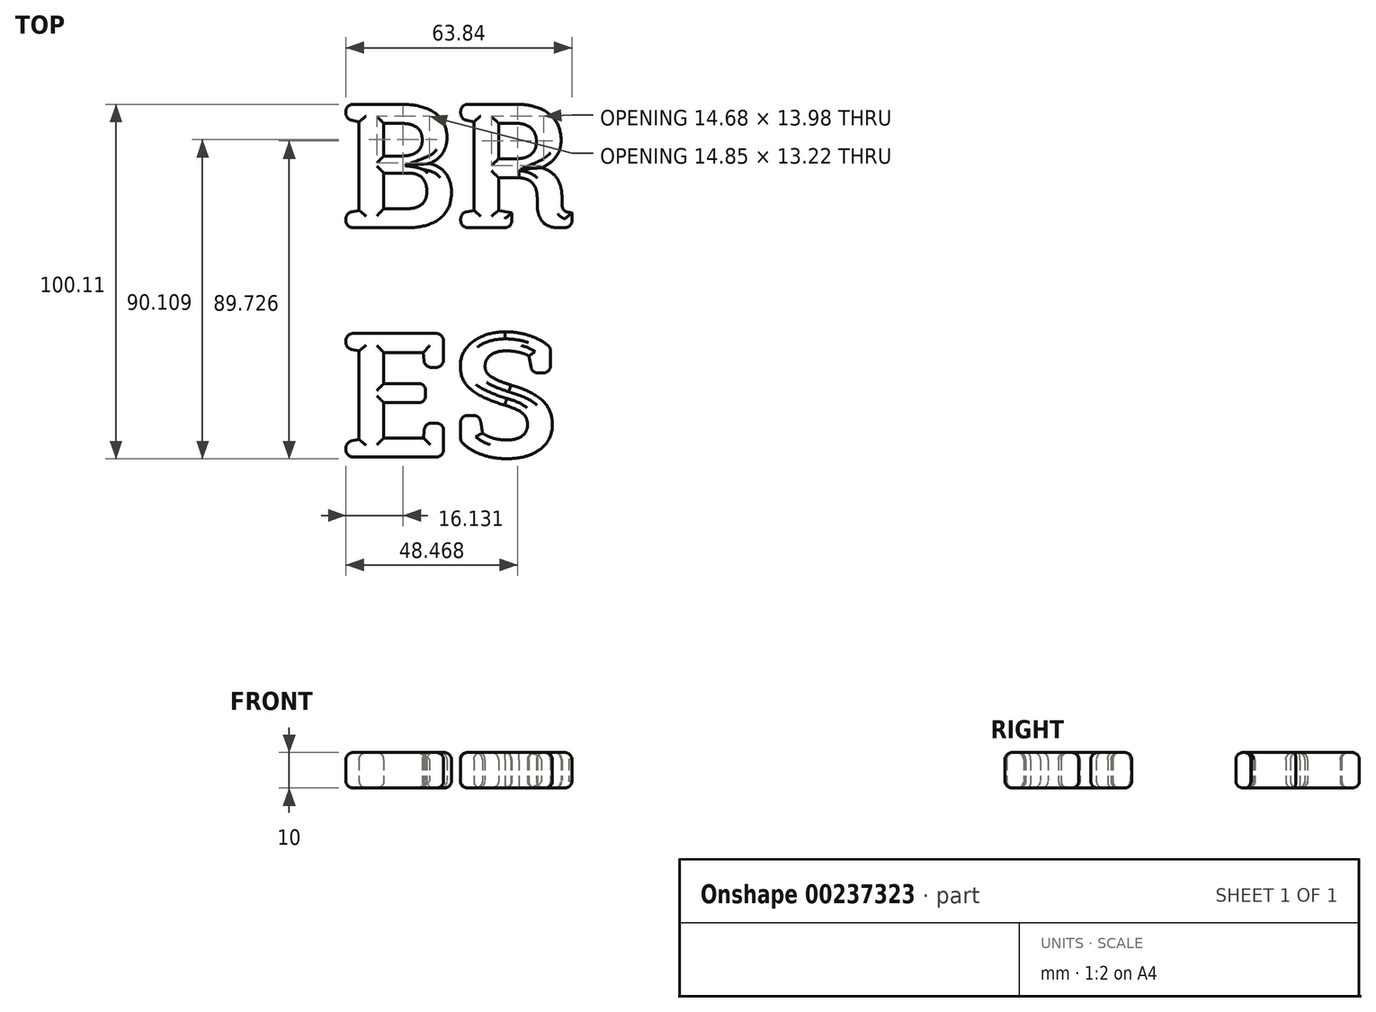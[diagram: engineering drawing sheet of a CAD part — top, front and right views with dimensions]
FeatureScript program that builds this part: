
annotation { "Feature Type Name" : "Feature", "Feature Type Description" : "" }
export const myFeature = defineFeature(function(context is Context, id is Id, definition is map)
    precondition{}
    {
        {
            var Q0;
            Q0=qCreatedBy(makeId("Top.planeOp"),FACE);
            var sketch = newSketch(context, id + "F0", { "sketchPlane" : qUnion([Q0])});
            skText(sketch, "E0", { "text": "BR\nES", "fontName": "RobotoSlab-Bold.ttf"});
            const initialGuessF0  = {"E0": [0, 0, 1, 0, 0.03531]};
            skSetInitialGuess(sketch, initialGuessF0);
            skSolve(sketch);
        }
        {
            var Q0;
            Q0 = qSketchRegion(id + "F0", true);
            extrude(context, id + "F1", {"entities" : qUnion([Q0]), "depth" : 10 * mm});
        }
        {
            var Q0;
            Q0=makeQuery(id+"F1.opExtrude","CAP_FACE",FACE,{"disambiguationData":[OSD([sQuery(id+"F0.wireOp",EDGE,"E0.sketch_text.stroke-0"),sQuery(id+"F0.wireOp",EDGE,"E0.sketch_text.stroke-1"),sQuery(id+"F0.wireOp",EDGE,"E0.sketch_text.stroke-2"),sQuery(id+"F0.wireOp",EDGE,"E0.sketch_text.stroke-3"),sQuery(id+"F0.wireOp",EDGE,"E0.sketch_text.stroke-4"),sQuery(id+"F0.wireOp",EDGE,"E0.sketch_text.stroke-5"),sQuery(id+"F0.wireOp",EDGE,"E0.sketch_text.stroke-6"),sQuery(id+"F0.wireOp",EDGE,"E0.sketch_text.stroke-7"),sQuery(id+"F0.wireOp",EDGE,"E0.sketch_text.stroke-8"),sQuery(id+"F0.wireOp",EDGE,"E0.sketch_text.stroke-9"),sQuery(id+"F0.wireOp",EDGE,"E0.sketch_text.stroke-10"),sQuery(id+"F0.wireOp",EDGE,"E0.sketch_text.stroke-11"),sQuery(id+"F0.wireOp",EDGE,"E0.sketch_text.stroke-12"),sQuery(id+"F0.wireOp",EDGE,"E0.sketch_text.stroke-13"),sQuery(id+"F0.wireOp",EDGE,"E0.sketch_text.stroke-14"),sQuery(id+"F0.wireOp",EDGE,"E0.sketch_text.stroke-15"),sQuery(id+"F0.wireOp",EDGE,"E0.sketch_text.stroke-16"),sQuery(id+"F0.wireOp",EDGE,"E0.sketch_text.stroke-17"),sQuery(id+"F0.wireOp",EDGE,"E0.sketch_text.stroke-18"),sQuery(id+"F0.wireOp",EDGE,"E0.sketch_text.stroke-19"),sQuery(id+"F0.wireOp",EDGE,"E0.sketch_text.stroke-20"),sQuery(id+"F0.wireOp",EDGE,"E0.sketch_text.stroke-21"),sQuery(id+"F0.wireOp",EDGE,"E0.sketch_text.stroke-22"),sQuery(id+"F0.wireOp",EDGE,"E0.sketch_text.stroke-23"),sQuery(id+"F0.wireOp",EDGE,"E0.sketch_text.stroke-24"),sQuery(id+"F0.wireOp",EDGE,"E0.sketch_text.stroke-25"),sQuery(id+"F0.wireOp",EDGE,"E0.sketch_text.stroke-26"),sQuery(id+"F0.wireOp",EDGE,"E0.sketch_text.stroke-27"),sQuery(id+"F0.wireOp",EDGE,"E0.sketch_text.stroke-28"),sQuery(id+"F0.wireOp",EDGE,"E0.sketch_text.stroke-29")])],"isStart":false});
            var Q1;
            Q1=makeQuery(id+"F1.opExtrude","CAP_FACE",FACE,{"disambiguationData":[OSD([sQuery(id+"F0.wireOp",EDGE,"E0.sketch_text.stroke-0"),sQuery(id+"F0.wireOp",EDGE,"E0.sketch_text.stroke-1"),sQuery(id+"F0.wireOp",EDGE,"E0.sketch_text.stroke-2"),sQuery(id+"F0.wireOp",EDGE,"E0.sketch_text.stroke-3"),sQuery(id+"F0.wireOp",EDGE,"E0.sketch_text.stroke-4"),sQuery(id+"F0.wireOp",EDGE,"E0.sketch_text.stroke-5"),sQuery(id+"F0.wireOp",EDGE,"E0.sketch_text.stroke-6"),sQuery(id+"F0.wireOp",EDGE,"E0.sketch_text.stroke-7"),sQuery(id+"F0.wireOp",EDGE,"E0.sketch_text.stroke-8"),sQuery(id+"F0.wireOp",EDGE,"E0.sketch_text.stroke-9"),sQuery(id+"F0.wireOp",EDGE,"E0.sketch_text.stroke-10"),sQuery(id+"F0.wireOp",EDGE,"E0.sketch_text.stroke-11"),sQuery(id+"F0.wireOp",EDGE,"E0.sketch_text.stroke-12"),sQuery(id+"F0.wireOp",EDGE,"E0.sketch_text.stroke-13"),sQuery(id+"F0.wireOp",EDGE,"E0.sketch_text.stroke-14"),sQuery(id+"F0.wireOp",EDGE,"E0.sketch_text.stroke-15"),sQuery(id+"F0.wireOp",EDGE,"E0.sketch_text.stroke-16"),sQuery(id+"F0.wireOp",EDGE,"E0.sketch_text.stroke-17"),sQuery(id+"F0.wireOp",EDGE,"E0.sketch_text.stroke-18"),sQuery(id+"F0.wireOp",EDGE,"E0.sketch_text.stroke-19"),sQuery(id+"F0.wireOp",EDGE,"E0.sketch_text.stroke-20"),sQuery(id+"F0.wireOp",EDGE,"E0.sketch_text.stroke-21"),sQuery(id+"F0.wireOp",EDGE,"E0.sketch_text.stroke-22"),sQuery(id+"F0.wireOp",EDGE,"E0.sketch_text.stroke-23"),sQuery(id+"F0.wireOp",EDGE,"E0.sketch_text.stroke-24"),sQuery(id+"F0.wireOp",EDGE,"E0.sketch_text.stroke-25"),sQuery(id+"F0.wireOp",EDGE,"E0.sketch_text.stroke-26"),sQuery(id+"F0.wireOp",EDGE,"E0.sketch_text.stroke-27"),sQuery(id+"F0.wireOp",EDGE,"E0.sketch_text.stroke-28"),sQuery(id+"F0.wireOp",EDGE,"E0.sketch_text.stroke-29")])],"isStart":true});
            var Q2;
            Q2=makeQuery(id+"F1.opExtrude","SWEPT_FACE",FACE,{"disambiguationData":[OSD([sQuery(id+"F0.wireOp",EDGE,"E0.sketch_text.stroke-13")])]});
            var Q3;
            Q3=makeQuery(id+"F1.opExtrude","SWEPT_FACE",FACE,{"disambiguationData":[OSD([sQuery(id+"F0.wireOp",EDGE,"E0.sketch_text.stroke-9")])]});
            var Q4;
            Q4=makeQuery(id+"F1.opExtrude","CAP_FACE",FACE,{"disambiguationData":[OSD([sQuery(id+"F0.wireOp",EDGE,"E0.sketch_text.stroke-30"),sQuery(id+"F0.wireOp",EDGE,"E0.sketch_text.stroke-31"),sQuery(id+"F0.wireOp",EDGE,"E0.sketch_text.stroke-32"),sQuery(id+"F0.wireOp",EDGE,"E0.sketch_text.stroke-33"),sQuery(id+"F0.wireOp",EDGE,"E0.sketch_text.stroke-34"),sQuery(id+"F0.wireOp",EDGE,"E0.sketch_text.stroke-35"),sQuery(id+"F0.wireOp",EDGE,"E0.sketch_text.stroke-36"),sQuery(id+"F0.wireOp",EDGE,"E0.sketch_text.stroke-37"),sQuery(id+"F0.wireOp",EDGE,"E0.sketch_text.stroke-38"),sQuery(id+"F0.wireOp",EDGE,"E0.sketch_text.stroke-39"),sQuery(id+"F0.wireOp",EDGE,"E0.sketch_text.stroke-40"),sQuery(id+"F0.wireOp",EDGE,"E0.sketch_text.stroke-41"),sQuery(id+"F0.wireOp",EDGE,"E0.sketch_text.stroke-42"),sQuery(id+"F0.wireOp",EDGE,"E0.sketch_text.stroke-43"),sQuery(id+"F0.wireOp",EDGE,"E0.sketch_text.stroke-44"),sQuery(id+"F0.wireOp",EDGE,"E0.sketch_text.stroke-45"),sQuery(id+"F0.wireOp",EDGE,"E0.sketch_text.stroke-46"),sQuery(id+"F0.wireOp",EDGE,"E0.sketch_text.stroke-47"),sQuery(id+"F0.wireOp",EDGE,"E0.sketch_text.stroke-48"),sQuery(id+"F0.wireOp",EDGE,"E0.sketch_text.stroke-49"),sQuery(id+"F0.wireOp",EDGE,"E0.sketch_text.stroke-50"),sQuery(id+"F0.wireOp",EDGE,"E0.sketch_text.stroke-51"),sQuery(id+"F0.wireOp",EDGE,"E0.sketch_text.stroke-52"),sQuery(id+"F0.wireOp",EDGE,"E0.sketch_text.stroke-53"),sQuery(id+"F0.wireOp",EDGE,"E0.sketch_text.stroke-54"),sQuery(id+"F0.wireOp",EDGE,"E0.sketch_text.stroke-55"),sQuery(id+"F0.wireOp",EDGE,"E0.sketch_text.stroke-56"),sQuery(id+"F0.wireOp",EDGE,"E0.sketch_text.stroke-57"),sQuery(id+"F0.wireOp",EDGE,"E0.sketch_text.stroke-58"),sQuery(id+"F0.wireOp",EDGE,"E0.sketch_text.stroke-59"),sQuery(id+"F0.wireOp",EDGE,"E0.sketch_text.stroke-60"),sQuery(id+"F0.wireOp",EDGE,"E0.sketch_text.stroke-61"),sQuery(id+"F0.wireOp",EDGE,"E0.sketch_text.stroke-62"),sQuery(id+"F0.wireOp",EDGE,"E0.sketch_text.stroke-63"),sQuery(id+"F0.wireOp",EDGE,"E0.sketch_text.stroke-64"),sQuery(id+"F0.wireOp",EDGE,"E0.sketch_text.stroke-65")])],"isStart":false});
            var Q5;
            Q5=makeQuery(id+"F1.opExtrude","CAP_FACE",FACE,{"disambiguationData":[OSD([sQuery(id+"F0.wireOp",EDGE,"E0.sketch_text.stroke-30"),sQuery(id+"F0.wireOp",EDGE,"E0.sketch_text.stroke-31"),sQuery(id+"F0.wireOp",EDGE,"E0.sketch_text.stroke-32"),sQuery(id+"F0.wireOp",EDGE,"E0.sketch_text.stroke-33"),sQuery(id+"F0.wireOp",EDGE,"E0.sketch_text.stroke-34"),sQuery(id+"F0.wireOp",EDGE,"E0.sketch_text.stroke-35"),sQuery(id+"F0.wireOp",EDGE,"E0.sketch_text.stroke-36"),sQuery(id+"F0.wireOp",EDGE,"E0.sketch_text.stroke-37"),sQuery(id+"F0.wireOp",EDGE,"E0.sketch_text.stroke-38"),sQuery(id+"F0.wireOp",EDGE,"E0.sketch_text.stroke-39"),sQuery(id+"F0.wireOp",EDGE,"E0.sketch_text.stroke-40"),sQuery(id+"F0.wireOp",EDGE,"E0.sketch_text.stroke-41"),sQuery(id+"F0.wireOp",EDGE,"E0.sketch_text.stroke-42"),sQuery(id+"F0.wireOp",EDGE,"E0.sketch_text.stroke-43"),sQuery(id+"F0.wireOp",EDGE,"E0.sketch_text.stroke-44"),sQuery(id+"F0.wireOp",EDGE,"E0.sketch_text.stroke-45"),sQuery(id+"F0.wireOp",EDGE,"E0.sketch_text.stroke-46"),sQuery(id+"F0.wireOp",EDGE,"E0.sketch_text.stroke-47"),sQuery(id+"F0.wireOp",EDGE,"E0.sketch_text.stroke-48"),sQuery(id+"F0.wireOp",EDGE,"E0.sketch_text.stroke-49"),sQuery(id+"F0.wireOp",EDGE,"E0.sketch_text.stroke-50"),sQuery(id+"F0.wireOp",EDGE,"E0.sketch_text.stroke-51"),sQuery(id+"F0.wireOp",EDGE,"E0.sketch_text.stroke-52"),sQuery(id+"F0.wireOp",EDGE,"E0.sketch_text.stroke-53"),sQuery(id+"F0.wireOp",EDGE,"E0.sketch_text.stroke-54"),sQuery(id+"F0.wireOp",EDGE,"E0.sketch_text.stroke-55"),sQuery(id+"F0.wireOp",EDGE,"E0.sketch_text.stroke-56"),sQuery(id+"F0.wireOp",EDGE,"E0.sketch_text.stroke-57"),sQuery(id+"F0.wireOp",EDGE,"E0.sketch_text.stroke-58"),sQuery(id+"F0.wireOp",EDGE,"E0.sketch_text.stroke-59"),sQuery(id+"F0.wireOp",EDGE,"E0.sketch_text.stroke-60"),sQuery(id+"F0.wireOp",EDGE,"E0.sketch_text.stroke-61"),sQuery(id+"F0.wireOp",EDGE,"E0.sketch_text.stroke-62"),sQuery(id+"F0.wireOp",EDGE,"E0.sketch_text.stroke-63"),sQuery(id+"F0.wireOp",EDGE,"E0.sketch_text.stroke-64"),sQuery(id+"F0.wireOp",EDGE,"E0.sketch_text.stroke-65")])],"isStart":true});
            var Q6;
            Q6=makeQuery(id+"F1.opExtrude","SWEPT_FACE",FACE,{"disambiguationData":[OSD([sQuery(id+"F0.wireOp",EDGE,"E0.sketch_text.stroke-51")])]});
            var Q7;
            Q7=makeQuery(id+"F1.opExtrude","SWEPT_FACE",FACE,{"disambiguationData":[OSD([sQuery(id+"F0.wireOp",EDGE,"E0.sketch_text.stroke-52")])]});
            var Q8;
            Q8=makeQuery(id+"F1.opExtrude","SWEPT_FACE",FACE,{"disambiguationData":[OSD([sQuery(id+"F0.wireOp",EDGE,"E0.sketch_text.stroke-56")])]});
            var Q9;
            Q9=makeQuery(id+"F1.opExtrude","SWEPT_EDGE",EDGE,{"disambiguationData":[OSD([sQuery(id+"F0.wireOp",EDGE,"E0.sketch_text.stroke-40"),sQuery(id+"F0.wireOp",EDGE,"E0.sketch_text.stroke-41")])]});
            var Q10;
            Q10=makeQuery(id+"F1.opExtrude","CAP_FACE",FACE,{"disambiguationData":[OSD([sQuery(id+"F0.wireOp",EDGE,"E0.sketch_text.stroke-66"),sQuery(id+"F0.wireOp",EDGE,"E0.sketch_text.stroke-67"),sQuery(id+"F0.wireOp",EDGE,"E0.sketch_text.stroke-68"),sQuery(id+"F0.wireOp",EDGE,"E0.sketch_text.stroke-69"),sQuery(id+"F0.wireOp",EDGE,"E0.sketch_text.stroke-70"),sQuery(id+"F0.wireOp",EDGE,"E0.sketch_text.stroke-71"),sQuery(id+"F0.wireOp",EDGE,"E0.sketch_text.stroke-72"),sQuery(id+"F0.wireOp",EDGE,"E0.sketch_text.stroke-73"),sQuery(id+"F0.wireOp",EDGE,"E0.sketch_text.stroke-74"),sQuery(id+"F0.wireOp",EDGE,"E0.sketch_text.stroke-75"),sQuery(id+"F0.wireOp",EDGE,"E0.sketch_text.stroke-76"),sQuery(id+"F0.wireOp",EDGE,"E0.sketch_text.stroke-77"),sQuery(id+"F0.wireOp",EDGE,"E0.sketch_text.stroke-78"),sQuery(id+"F0.wireOp",EDGE,"E0.sketch_text.stroke-79"),sQuery(id+"F0.wireOp",EDGE,"E0.sketch_text.stroke-80"),sQuery(id+"F0.wireOp",EDGE,"E0.sketch_text.stroke-81"),sQuery(id+"F0.wireOp",EDGE,"E0.sketch_text.stroke-82"),sQuery(id+"F0.wireOp",EDGE,"E0.sketch_text.stroke-83"),sQuery(id+"F0.wireOp",EDGE,"E0.sketch_text.stroke-84"),sQuery(id+"F0.wireOp",EDGE,"E0.sketch_text.stroke-85"),sQuery(id+"F0.wireOp",EDGE,"E0.sketch_text.stroke-86")])],"isStart":false});
            var Q11;
            Q11=makeQuery(id+"F1.opExtrude","CAP_FACE",FACE,{"disambiguationData":[OSD([sQuery(id+"F0.wireOp",EDGE,"E0.sketch_text.stroke-87"),sQuery(id+"F0.wireOp",EDGE,"E0.sketch_text.stroke-88"),sQuery(id+"F0.wireOp",EDGE,"E0.sketch_text.stroke-89"),sQuery(id+"F0.wireOp",EDGE,"E0.sketch_text.stroke-90"),sQuery(id+"F0.wireOp",EDGE,"E0.sketch_text.stroke-91"),sQuery(id+"F0.wireOp",EDGE,"E0.sketch_text.stroke-92"),sQuery(id+"F0.wireOp",EDGE,"E0.sketch_text.stroke-93"),sQuery(id+"F0.wireOp",EDGE,"E0.sketch_text.stroke-94"),sQuery(id+"F0.wireOp",EDGE,"E0.sketch_text.stroke-95"),sQuery(id+"F0.wireOp",EDGE,"E0.sketch_text.stroke-96"),sQuery(id+"F0.wireOp",EDGE,"E0.sketch_text.stroke-97"),sQuery(id+"F0.wireOp",EDGE,"E0.sketch_text.stroke-98"),sQuery(id+"F0.wireOp",EDGE,"E0.sketch_text.stroke-99"),sQuery(id+"F0.wireOp",EDGE,"E0.sketch_text.stroke-100"),sQuery(id+"F0.wireOp",EDGE,"E0.sketch_text.stroke-101"),sQuery(id+"F0.wireOp",EDGE,"E0.sketch_text.stroke-102"),sQuery(id+"F0.wireOp",EDGE,"E0.sketch_text.stroke-103"),sQuery(id+"F0.wireOp",EDGE,"E0.sketch_text.stroke-104"),sQuery(id+"F0.wireOp",EDGE,"E0.sketch_text.stroke-105"),sQuery(id+"F0.wireOp",EDGE,"E0.sketch_text.stroke-106"),sQuery(id+"F0.wireOp",EDGE,"E0.sketch_text.stroke-107"),sQuery(id+"F0.wireOp",EDGE,"E0.sketch_text.stroke-108"),sQuery(id+"F0.wireOp",EDGE,"E0.sketch_text.stroke-109"),sQuery(id+"F0.wireOp",EDGE,"E0.sketch_text.stroke-110"),sQuery(id+"F0.wireOp",EDGE,"E0.sketch_text.stroke-111"),sQuery(id+"F0.wireOp",EDGE,"E0.sketch_text.stroke-112"),sQuery(id+"F0.wireOp",EDGE,"E0.sketch_text.stroke-113"),sQuery(id+"F0.wireOp",EDGE,"E0.sketch_text.stroke-114"),sQuery(id+"F0.wireOp",EDGE,"E0.sketch_text.stroke-115"),sQuery(id+"F0.wireOp",EDGE,"E0.sketch_text.stroke-116")])],"isStart":false});
            var Q12;
            Q12=makeQuery(id+"F1.opExtrude","CAP_FACE",FACE,{"disambiguationData":[OSD([sQuery(id+"F0.wireOp",EDGE,"E0.sketch_text.stroke-117"),sQuery(id+"F0.wireOp",EDGE,"E0.sketch_text.stroke-118"),sQuery(id+"F0.wireOp",EDGE,"E0.sketch_text.stroke-119"),sQuery(id+"F0.wireOp",EDGE,"E0.sketch_text.stroke-120"),sQuery(id+"F0.wireOp",EDGE,"E0.sketch_text.stroke-121"),sQuery(id+"F0.wireOp",EDGE,"E0.sketch_text.stroke-122"),sQuery(id+"F0.wireOp",EDGE,"E0.sketch_text.stroke-123"),sQuery(id+"F0.wireOp",EDGE,"E0.sketch_text.stroke-124"),sQuery(id+"F0.wireOp",EDGE,"E0.sketch_text.stroke-125"),sQuery(id+"F0.wireOp",EDGE,"E0.sketch_text.stroke-126"),sQuery(id+"F0.wireOp",EDGE,"E0.sketch_text.stroke-127"),sQuery(id+"F0.wireOp",EDGE,"E0.sketch_text.stroke-128"),sQuery(id+"F0.wireOp",EDGE,"E0.sketch_text.stroke-129"),sQuery(id+"F0.wireOp",EDGE,"E0.sketch_text.stroke-130"),sQuery(id+"F0.wireOp",EDGE,"E0.sketch_text.stroke-131"),sQuery(id+"F0.wireOp",EDGE,"E0.sketch_text.stroke-132"),sQuery(id+"F0.wireOp",EDGE,"E0.sketch_text.stroke-133"),sQuery(id+"F0.wireOp",EDGE,"E0.sketch_text.stroke-134"),sQuery(id+"F0.wireOp",EDGE,"E0.sketch_text.stroke-135"),sQuery(id+"F0.wireOp",EDGE,"E0.sketch_text.stroke-136"),sQuery(id+"F0.wireOp",EDGE,"E0.sketch_text.stroke-137"),sQuery(id+"F0.wireOp",EDGE,"E0.sketch_text.stroke-138"),sQuery(id+"F0.wireOp",EDGE,"E0.sketch_text.stroke-139"),sQuery(id+"F0.wireOp",EDGE,"E0.sketch_text.stroke-140"),sQuery(id+"F0.wireOp",EDGE,"E0.sketch_text.stroke-141"),sQuery(id+"F0.wireOp",EDGE,"E0.sketch_text.stroke-142"),sQuery(id+"F0.wireOp",EDGE,"E0.sketch_text.stroke-143"),sQuery(id+"F0.wireOp",EDGE,"E0.sketch_text.stroke-144"),sQuery(id+"F0.wireOp",EDGE,"E0.sketch_text.stroke-145"),sQuery(id+"F0.wireOp",EDGE,"E0.sketch_text.stroke-146")])],"isStart":false});
            var Q13;
            Q13=makeQuery(id+"F1.opExtrude","CAP_FACE",FACE,{"disambiguationData":[OSD([sQuery(id+"F0.wireOp",EDGE,"E0.sketch_text.stroke-66"),sQuery(id+"F0.wireOp",EDGE,"E0.sketch_text.stroke-67"),sQuery(id+"F0.wireOp",EDGE,"E0.sketch_text.stroke-68"),sQuery(id+"F0.wireOp",EDGE,"E0.sketch_text.stroke-69"),sQuery(id+"F0.wireOp",EDGE,"E0.sketch_text.stroke-70"),sQuery(id+"F0.wireOp",EDGE,"E0.sketch_text.stroke-71"),sQuery(id+"F0.wireOp",EDGE,"E0.sketch_text.stroke-72"),sQuery(id+"F0.wireOp",EDGE,"E0.sketch_text.stroke-73"),sQuery(id+"F0.wireOp",EDGE,"E0.sketch_text.stroke-74"),sQuery(id+"F0.wireOp",EDGE,"E0.sketch_text.stroke-75"),sQuery(id+"F0.wireOp",EDGE,"E0.sketch_text.stroke-76"),sQuery(id+"F0.wireOp",EDGE,"E0.sketch_text.stroke-77"),sQuery(id+"F0.wireOp",EDGE,"E0.sketch_text.stroke-78"),sQuery(id+"F0.wireOp",EDGE,"E0.sketch_text.stroke-79"),sQuery(id+"F0.wireOp",EDGE,"E0.sketch_text.stroke-80"),sQuery(id+"F0.wireOp",EDGE,"E0.sketch_text.stroke-81"),sQuery(id+"F0.wireOp",EDGE,"E0.sketch_text.stroke-82"),sQuery(id+"F0.wireOp",EDGE,"E0.sketch_text.stroke-83"),sQuery(id+"F0.wireOp",EDGE,"E0.sketch_text.stroke-84"),sQuery(id+"F0.wireOp",EDGE,"E0.sketch_text.stroke-85"),sQuery(id+"F0.wireOp",EDGE,"E0.sketch_text.stroke-86")])],"isStart":true});
            var Q14;
            Q14=makeQuery(id+"F1.opExtrude","CAP_FACE",FACE,{"disambiguationData":[OSD([sQuery(id+"F0.wireOp",EDGE,"E0.sketch_text.stroke-87"),sQuery(id+"F0.wireOp",EDGE,"E0.sketch_text.stroke-88"),sQuery(id+"F0.wireOp",EDGE,"E0.sketch_text.stroke-89"),sQuery(id+"F0.wireOp",EDGE,"E0.sketch_text.stroke-90"),sQuery(id+"F0.wireOp",EDGE,"E0.sketch_text.stroke-91"),sQuery(id+"F0.wireOp",EDGE,"E0.sketch_text.stroke-92"),sQuery(id+"F0.wireOp",EDGE,"E0.sketch_text.stroke-93"),sQuery(id+"F0.wireOp",EDGE,"E0.sketch_text.stroke-94"),sQuery(id+"F0.wireOp",EDGE,"E0.sketch_text.stroke-95"),sQuery(id+"F0.wireOp",EDGE,"E0.sketch_text.stroke-96"),sQuery(id+"F0.wireOp",EDGE,"E0.sketch_text.stroke-97"),sQuery(id+"F0.wireOp",EDGE,"E0.sketch_text.stroke-98"),sQuery(id+"F0.wireOp",EDGE,"E0.sketch_text.stroke-99"),sQuery(id+"F0.wireOp",EDGE,"E0.sketch_text.stroke-100"),sQuery(id+"F0.wireOp",EDGE,"E0.sketch_text.stroke-101"),sQuery(id+"F0.wireOp",EDGE,"E0.sketch_text.stroke-102"),sQuery(id+"F0.wireOp",EDGE,"E0.sketch_text.stroke-103"),sQuery(id+"F0.wireOp",EDGE,"E0.sketch_text.stroke-104"),sQuery(id+"F0.wireOp",EDGE,"E0.sketch_text.stroke-105"),sQuery(id+"F0.wireOp",EDGE,"E0.sketch_text.stroke-106"),sQuery(id+"F0.wireOp",EDGE,"E0.sketch_text.stroke-107"),sQuery(id+"F0.wireOp",EDGE,"E0.sketch_text.stroke-108"),sQuery(id+"F0.wireOp",EDGE,"E0.sketch_text.stroke-109"),sQuery(id+"F0.wireOp",EDGE,"E0.sketch_text.stroke-110"),sQuery(id+"F0.wireOp",EDGE,"E0.sketch_text.stroke-111"),sQuery(id+"F0.wireOp",EDGE,"E0.sketch_text.stroke-112"),sQuery(id+"F0.wireOp",EDGE,"E0.sketch_text.stroke-113"),sQuery(id+"F0.wireOp",EDGE,"E0.sketch_text.stroke-114"),sQuery(id+"F0.wireOp",EDGE,"E0.sketch_text.stroke-115"),sQuery(id+"F0.wireOp",EDGE,"E0.sketch_text.stroke-116")])],"isStart":true});
            var Q15;
            Q15=makeQuery(id+"F1.opExtrude","CAP_FACE",FACE,{"disambiguationData":[OSD([sQuery(id+"F0.wireOp",EDGE,"E0.sketch_text.stroke-117"),sQuery(id+"F0.wireOp",EDGE,"E0.sketch_text.stroke-118"),sQuery(id+"F0.wireOp",EDGE,"E0.sketch_text.stroke-119"),sQuery(id+"F0.wireOp",EDGE,"E0.sketch_text.stroke-120"),sQuery(id+"F0.wireOp",EDGE,"E0.sketch_text.stroke-121"),sQuery(id+"F0.wireOp",EDGE,"E0.sketch_text.stroke-122"),sQuery(id+"F0.wireOp",EDGE,"E0.sketch_text.stroke-123"),sQuery(id+"F0.wireOp",EDGE,"E0.sketch_text.stroke-124"),sQuery(id+"F0.wireOp",EDGE,"E0.sketch_text.stroke-125"),sQuery(id+"F0.wireOp",EDGE,"E0.sketch_text.stroke-126"),sQuery(id+"F0.wireOp",EDGE,"E0.sketch_text.stroke-127"),sQuery(id+"F0.wireOp",EDGE,"E0.sketch_text.stroke-128"),sQuery(id+"F0.wireOp",EDGE,"E0.sketch_text.stroke-129"),sQuery(id+"F0.wireOp",EDGE,"E0.sketch_text.stroke-130"),sQuery(id+"F0.wireOp",EDGE,"E0.sketch_text.stroke-131"),sQuery(id+"F0.wireOp",EDGE,"E0.sketch_text.stroke-132"),sQuery(id+"F0.wireOp",EDGE,"E0.sketch_text.stroke-133"),sQuery(id+"F0.wireOp",EDGE,"E0.sketch_text.stroke-134"),sQuery(id+"F0.wireOp",EDGE,"E0.sketch_text.stroke-135"),sQuery(id+"F0.wireOp",EDGE,"E0.sketch_text.stroke-136"),sQuery(id+"F0.wireOp",EDGE,"E0.sketch_text.stroke-137"),sQuery(id+"F0.wireOp",EDGE,"E0.sketch_text.stroke-138"),sQuery(id+"F0.wireOp",EDGE,"E0.sketch_text.stroke-139"),sQuery(id+"F0.wireOp",EDGE,"E0.sketch_text.stroke-140"),sQuery(id+"F0.wireOp",EDGE,"E0.sketch_text.stroke-141"),sQuery(id+"F0.wireOp",EDGE,"E0.sketch_text.stroke-142"),sQuery(id+"F0.wireOp",EDGE,"E0.sketch_text.stroke-143"),sQuery(id+"F0.wireOp",EDGE,"E0.sketch_text.stroke-144"),sQuery(id+"F0.wireOp",EDGE,"E0.sketch_text.stroke-145"),sQuery(id+"F0.wireOp",EDGE,"E0.sketch_text.stroke-146")])],"isStart":true});
            var Q16;
            Q16=makeQuery(id+"F1.opExtrude","SWEPT_FACE",FACE,{"disambiguationData":[OSD([sQuery(id+"F0.wireOp",EDGE,"E0.sketch_text.stroke-102")])]});
            var Q17;
            Q17=makeQuery(id+"F1.opExtrude","SWEPT_FACE",FACE,{"disambiguationData":[OSD([sQuery(id+"F0.wireOp",EDGE,"E0.sketch_text.stroke-87")])]});
            var Q18;
            Q18=makeQuery(id+"F1.opExtrude","SWEPT_FACE",FACE,{"disambiguationData":[OSD([sQuery(id+"F0.wireOp",EDGE,"E0.sketch_text.stroke-101")])]});
            var Q19;
            Q19=makeQuery(id+"F1.opExtrude","SWEPT_FACE",FACE,{"disambiguationData":[OSD([sQuery(id+"F0.wireOp",EDGE,"E0.sketch_text.stroke-116")])]});
            var Q20;
            Q20=makeQuery(id+"F1.opExtrude","SWEPT_FACE",FACE,{"disambiguationData":[OSD([sQuery(id+"F0.wireOp",EDGE,"E0.sketch_text.stroke-72")])]});
            var Q21;
            Q21=makeQuery(id+"F1.opExtrude","SWEPT_FACE",FACE,{"disambiguationData":[OSD([sQuery(id+"F0.wireOp",EDGE,"E0.sketch_text.stroke-81")])]});
            var Q22;
            Q22=makeQuery(id+"F1.opExtrude","SWEPT_FACE",FACE,{"disambiguationData":[OSD([sQuery(id+"F0.wireOp",EDGE,"E0.sketch_text.stroke-78"),sQuery(id+"F0.wireOp",EDGE,"E0.sketch_text.stroke-79")])]});
            var Q23;
            Q23=makeQuery(id+"F1.opExtrude","SWEPT_FACE",FACE,{"disambiguationData":[OSD([sQuery(id+"F0.wireOp",EDGE,"E0.sketch_text.stroke-70")])]});
            var Q24;
            Q24=makeQuery(id+"F1.opExtrude","SWEPT_EDGE",EDGE,{"disambiguationData":[OSD([sQuery(id+"F0.wireOp",EDGE,"E0.sketch_text.stroke-76"),sQuery(id+"F0.wireOp",EDGE,"E0.sketch_text.stroke-77")])]});
            var Q25;
            Q25=makeQuery(id+"F1.opExtrude","SWEPT_FACE",FACE,{"disambiguationData":[OSD([sQuery(id+"F0.wireOp",EDGE,"E0.sketch_text.stroke-73")])]});
            var Q26;
            Q26=makeQuery(id+"F1.opExtrude","SWEPT_FACE",FACE,{"disambiguationData":[OSD([sQuery(id+"F0.wireOp",EDGE,"E0.sketch_text.stroke-86")])]});
            fillet(context, id + "F2", {"entities" : qUnion([Q0, Q1, Q2, Q3, Q4, Q5, Q6, Q7, Q8, Q9, Q10, Q11, Q12, Q13, Q14, Q15, Q16, Q17, Q18, Q19, Q20, Q21, Q22, Q23, Q24, Q25, Q26]), "radius" : 2 * mm, "tangentPropagation" : true, "allowEdgeOverflow" : false});
        }
    });
